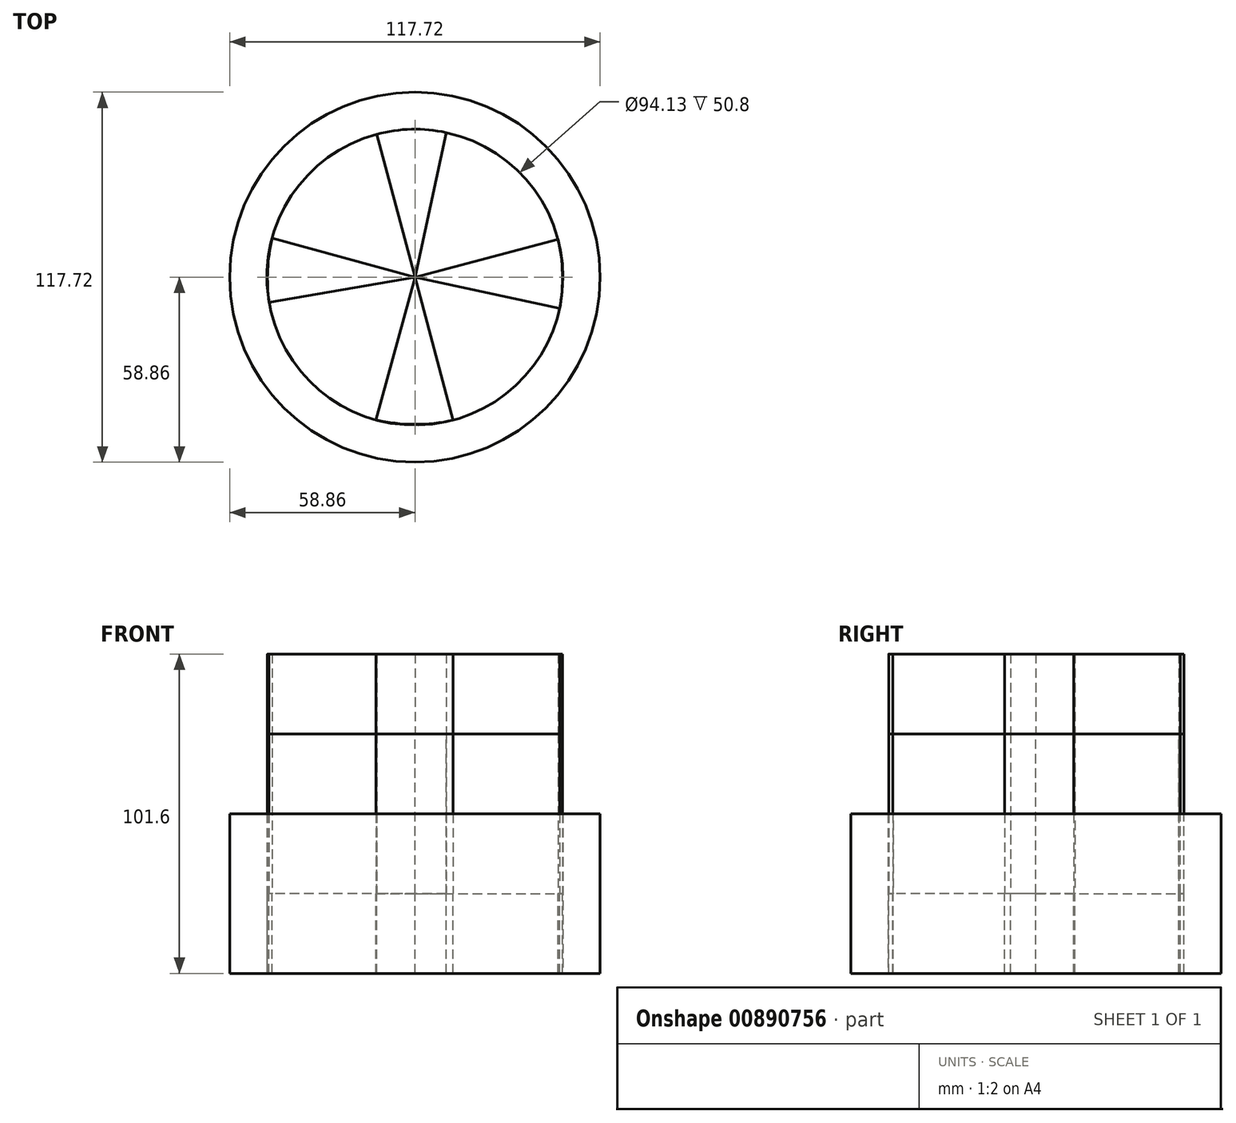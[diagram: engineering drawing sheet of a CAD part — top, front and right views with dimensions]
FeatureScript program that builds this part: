
annotation { "Feature Type Name" : "Feature", "Feature Type Description" : "" }
export const myFeature = defineFeature(function(context is Context, id is Id, definition is map)
    precondition{}
    {
        {
            var Q0;
            Q0=qCreatedBy(makeId("Top.planeOp"),FACE);
            var sketch = newSketch(context, id + "F0", { "sketchPlane" : qUnion([Q0])});
            skCircle(sketch, "E0", {"center": v(0, 0) * mm, "radius": 58.86 * mm});
            skCircle(sketch, "E1", {"center": v(0, 0) * mm, "radius": 47.07 * mm});
            skSolve(sketch);
        }
        {
            var Q0;
            Q0 = qSketchRegion(id + "F0", true);
            extrude(context, id + "F1", {"entities" : qUnion([Q0]), "depth" : 50.8 * mm, "offsetDistance" : 25.4 * mm});
        }
        {
            var Q0;
            Q0=makeQuery(id+"F1.opExtrude","CAP_FACE",FACE,{"disambiguationData":[OSD([sQuery(id+"F0.wireOp",EDGE,"E0"),sQuery(id+"F0.wireOp",EDGE,"E1")])],"isStart":false});
            var sketch = newSketch(context, id + "F2", { "sketchPlane" : qUnion([Q0])});
            skLineSegment(sketch, "E2", {"start": v(0, 0) * mm, "end": v(-12.1, 45.48) * mm});
            skLineSegment(sketch, "E3", {"start": v(0, 0) * mm, "end": v(9.95, 46) * mm});
            skArc(sketch, "E4", {"start": v(9.95, 46) * mm, "mid": v(-1.1, 47.1) * mm, "end": v(-12.1, 45.48) * mm});
            skLineSegment(sketch, "E5", {"start": v(0, 0) * mm, "end": v(-12.43, -45.4) * mm});
            skLineSegment(sketch, "E6", {"start": v(0, 0) * mm, "end": v(12.1, -45.48) * mm});
            skArc(sketch, "E7", {"start": v(-12.43, -45.4) * mm, "mid": v(-0.17, -46.8) * mm, "end": v(12.1, -45.48) * mm});
            skLineSegment(sketch, "E8", {"start": v(0, 0) * mm, "end": v(45.48, 12.1) * mm});
            skLineSegment(sketch, "E9", {"start": v(0, 0) * mm, "end": v(46, -9.95) * mm});
            skArc(sketch, "E10", {"start": v(46, -9.95) * mm, "mid": v(46.9, 1.1) * mm, "end": v(45.48, 12.1) * mm});
            skLineSegment(sketch, "E11", {"start": v(0, 0) * mm, "end": v(-45.4, 12.43) * mm});
            skLineSegment(sketch, "E12", {"start": v(0, 0) * mm, "end": v(-46.39, -7.98) * mm});
            skArc(sketch, "E13", {"start": v(-45.4, 12.43) * mm, "mid": v(-46.8, 2.27) * mm, "end": v(-46.39, -7.98) * mm});
            skSolve(sketch);
        }
        {
            var Q0;
            {var subQ0=sQuery(id+"F2.wireOp",EDGE,"E2");Q0=makeQuery(id+"F2.imprint","IMPRINT",FACE,{"disambiguationData":[TD([[makeQuery(id+"F2.imprint","IMPRINT",EDGE,{"derivedFrom":subQ0}),-1.0]])]});}
            var Q1;
            Q1=makeQuery(id+"F2.imprint","IMPRINT",FACE,{"disambiguationData":[TD([[makeQuery(id+"F2.imprint","IMPRINT",EDGE,{"derivedFrom":sQuery(id+"F2.wireOp",EDGE,"E8")}),-1.0]])]});
            var Q2;
            Q2=makeQuery(id+"F2.imprint","IMPRINT",FACE,{"disambiguationData":[TD([[makeQuery(id+"F2.imprint","IMPRINT",EDGE,{"derivedFrom":sQuery(id+"F2.wireOp",EDGE,"E5")}),1.0]])]});
            var Q3;
            Q3=makeQuery(id+"F2.imprint","IMPRINT",FACE,{"disambiguationData":[TD([[makeQuery(id+"F2.imprint","IMPRINT",EDGE,{"derivedFrom":sQuery(id+"F2.wireOp",EDGE,"E11")}),1.0]])]});
            extrude(context, id + "F3", {"entities" : qUnion([Q0, Q1, Q2, Q3]), "operationType" : NewBodyOperationType.ADD, "endBound" : BoundingType.SYMMETRIC, "depth" : 50.8 * mm, "offsetDistance" : 25.4 * mm});
        }
        {
            var Q0;
            Q0=makeQuery(id+"F3.opExtrude","CAP_FACE",FACE,{"disambiguationData":[OSD([sQuery(id+"F0.wireOp",EDGE,"E1"),sQuery(id+"F2.wireOp",EDGE,"E2"),sQuery(id+"F2.wireOp",EDGE,"E3")])],"isStart":false});
            var Q1;
            Q1=makeQuery(id+"F3.opExtrude","CAP_FACE",FACE,{"disambiguationData":[OSD([sQuery(id+"F2.wireOp",EDGE,"E11"),sQuery(id+"F2.wireOp",EDGE,"E12"),sQuery(id+"F2.wireOp",EDGE,"E13")])],"isStart":false});
            var Q2;
            Q2=makeQuery(id+"F3.opExtrude","CAP_FACE",FACE,{"disambiguationData":[OSD([sQuery(id+"F2.wireOp",EDGE,"E5"),sQuery(id+"F2.wireOp",EDGE,"E6"),sQuery(id+"F2.wireOp",EDGE,"E7")])],"isStart":false});
            var Q3;
            Q3=makeQuery(id+"F3.opExtrude","CAP_FACE",FACE,{"disambiguationData":[OSD([sQuery(id+"F2.wireOp",EDGE,"E8"),sQuery(id+"F2.wireOp",EDGE,"E9"),sQuery(id+"F2.wireOp",EDGE,"E10")])],"isStart":false});
            extrude(context, id + "F4", {"entities" : qUnion([Q0, Q1, Q2, Q3]), "oppositeDirection" : true, "depth" : 50.8 * mm, "offsetDistance" : 25.4 * mm});
        }
        {
            var Q0;
            Q0=makeQuery(id+"F3.opExtrude","CAP_FACE",FACE,{"disambiguationData":[OSD([sQuery(id+"F2.wireOp",EDGE,"E8"),sQuery(id+"F2.wireOp",EDGE,"E9"),sQuery(id+"F2.wireOp",EDGE,"E10")])],"isStart":true});
            var Q1;
            Q1=makeQuery(id+"F3.opExtrude","CAP_FACE",FACE,{"disambiguationData":[OSD([sQuery(id+"F2.wireOp",EDGE,"E5"),sQuery(id+"F2.wireOp",EDGE,"E6"),sQuery(id+"F2.wireOp",EDGE,"E7")])],"isStart":true});
            var Q2;
            Q2=makeQuery(id+"F3.opExtrude","CAP_FACE",FACE,{"disambiguationData":[OSD([sQuery(id+"F2.wireOp",EDGE,"E11"),sQuery(id+"F2.wireOp",EDGE,"E12"),sQuery(id+"F2.wireOp",EDGE,"E13")])],"isStart":true});
            var Q3;
            Q3=makeQuery(id+"F3.opExtrude","CAP_FACE",FACE,{"disambiguationData":[OSD([sQuery(id+"F0.wireOp",EDGE,"E1"),sQuery(id+"F2.wireOp",EDGE,"E2"),sQuery(id+"F2.wireOp",EDGE,"E3")])],"isStart":true});
            extrude(context, id + "F5", {"entities" : qUnion([Q0, Q1, Q2, Q3]), "depth" : 25.4 * mm, "offsetDistance" : 25.4 * mm});
        }
        {
            var Q0;
            Q0=makeQuery(id+"F4.opExtrude","CAP_FACE",FACE,{"disambiguationData":[OSD([sQuery(id+"F2.wireOp",EDGE,"E8"),sQuery(id+"F2.wireOp",EDGE,"E9"),sQuery(id+"F2.wireOp",EDGE,"E10")])],"isStart":true});
            var Q1;
            Q1=makeQuery(id+"F3.opExtrude","CAP_FACE",FACE,{"disambiguationData":[OSD([sQuery(id+"F2.wireOp",EDGE,"E5"),sQuery(id+"F2.wireOp",EDGE,"E6"),sQuery(id+"F2.wireOp",EDGE,"E7")])],"isStart":false});
            var Q2;
            Q2=makeQuery(id+"F3.opExtrude","CAP_FACE",FACE,{"disambiguationData":[OSD([sQuery(id+"F2.wireOp",EDGE,"E11"),sQuery(id+"F2.wireOp",EDGE,"E12"),sQuery(id+"F2.wireOp",EDGE,"E13")])],"isStart":false});
            var Q3;
            Q3=makeQuery(id+"F3.opExtrude","CAP_FACE",FACE,{"disambiguationData":[OSD([sQuery(id+"F0.wireOp",EDGE,"E1"),sQuery(id+"F2.wireOp",EDGE,"E2"),sQuery(id+"F2.wireOp",EDGE,"E3")])],"isStart":false});
            extrude(context, id + "F6", {"entities" : qUnion([Q0, Q1, Q2, Q3]), "depth" : 25.4 * mm, "offsetDistance" : 25.4 * mm});
        }
    });
